# Revit family: BE_88164_de_DE
name_source: partatom
category: Leuchten
revit_build: Autodesk Revit 2015 (Build: 20150704_0715(x64)
units: mm (PartAtom-declared; Revit-internal decimal feet)

## types (4) — shared parameters
AC/DC = AC
Aktualisierung = 2016-01-22T11:37:27
Anschlussleitung = 6.0 m X05BQ-F 5 G 1²
BEGA_Dummy = Nein
BEGA_IES = Ja
BEGA_Intern = Ja
BEGA_Intern_Konstruktion = Ja
BEGA_Intern_an = Ja
BEGA_Intern_aus = Ja
Beschreibung = Aufsatzleuchte
Beschreibung_Sonderanfertigung = Hier können Sie Informationen zur Sonderanfertigung eintragen.
CE_Konformität = ja
ENEC = ja
Einstecktiefe = 85 mm
Energieeffizienzklasse = LED A++ - A
Farbfilter = 16777215
Farbtemperaturverschiebung bei Dämpfen der Lampe = <Keine Auswahl>
Farbwiedergabeindex = Ra > 80
Frequenz = 50-60 Hz
Gewicht = 6.05 kg
Hersteller = BEGA
Lampe = LED 25.2 W
Lastklassifizierung = Beleuchtung
Lebensdauerkriterien = L70 = 50.000 h
Logo = BEGA_Logo.png
M_W = Nein
Material_02 = BEGA_Oberfläche_Silber_matt
Material_06 = BEGA_Oberfläche_Edelstahl_gebürstet
Material_14 = BEGA_Kunststoff_opal
Neigungswinkel = 0.00°
Produktdatenblatt = http://www.bega.de
Scheinlast = 0 VA
Schutzart = IP 65
Schutzklasse = I
Sonderanfertigung = Nein
Spannung = 0 V
Typenbild = 88164.png
URL = http://www.bega.de
Umgebungstemperatur = 25 °C
Windangriffsfläche = 0.06 m²
zero-valued in all types: Vorgabe-Ansicht

## per-type parameters (varying)
| type | Bestellnummer | Datei für fotometrisches Netz | Farbtemperatur | LED_Modulbezeichnung | Lampenlichtstrom | Leuchtenlichtstrom | M_A | M_G | Modell |
| BEGA_88164_Silber_K3 | 88164AK3 | BE_88164K3.IES | 3000 K | 4x LED-0601/830 | 3400 lm | 2325 lm | Ja | Nein | 88164AK3 |
| BEGA_88164_Silber_K4 | 88164A | BE_88164.IES | 4000 K | 4x LED-0601/840 | 3700 lm | 2531 lm | Ja | Nein | 88164A |
| BEGA_88164_Grafit_K4 | 88164 | BE_88164.IES | 4000 K | 4x LED-0601/840 | 3700 lm | 2531 lm | Nein | Ja | 88164 |
| BEGA_88164_Grafit_K3 | 88164K3 | BE_88164K3.IES | 3000 K | 4x LED-0601/830 | 3400 lm | 2325 lm | Nein | Ja | 88164K3 |
